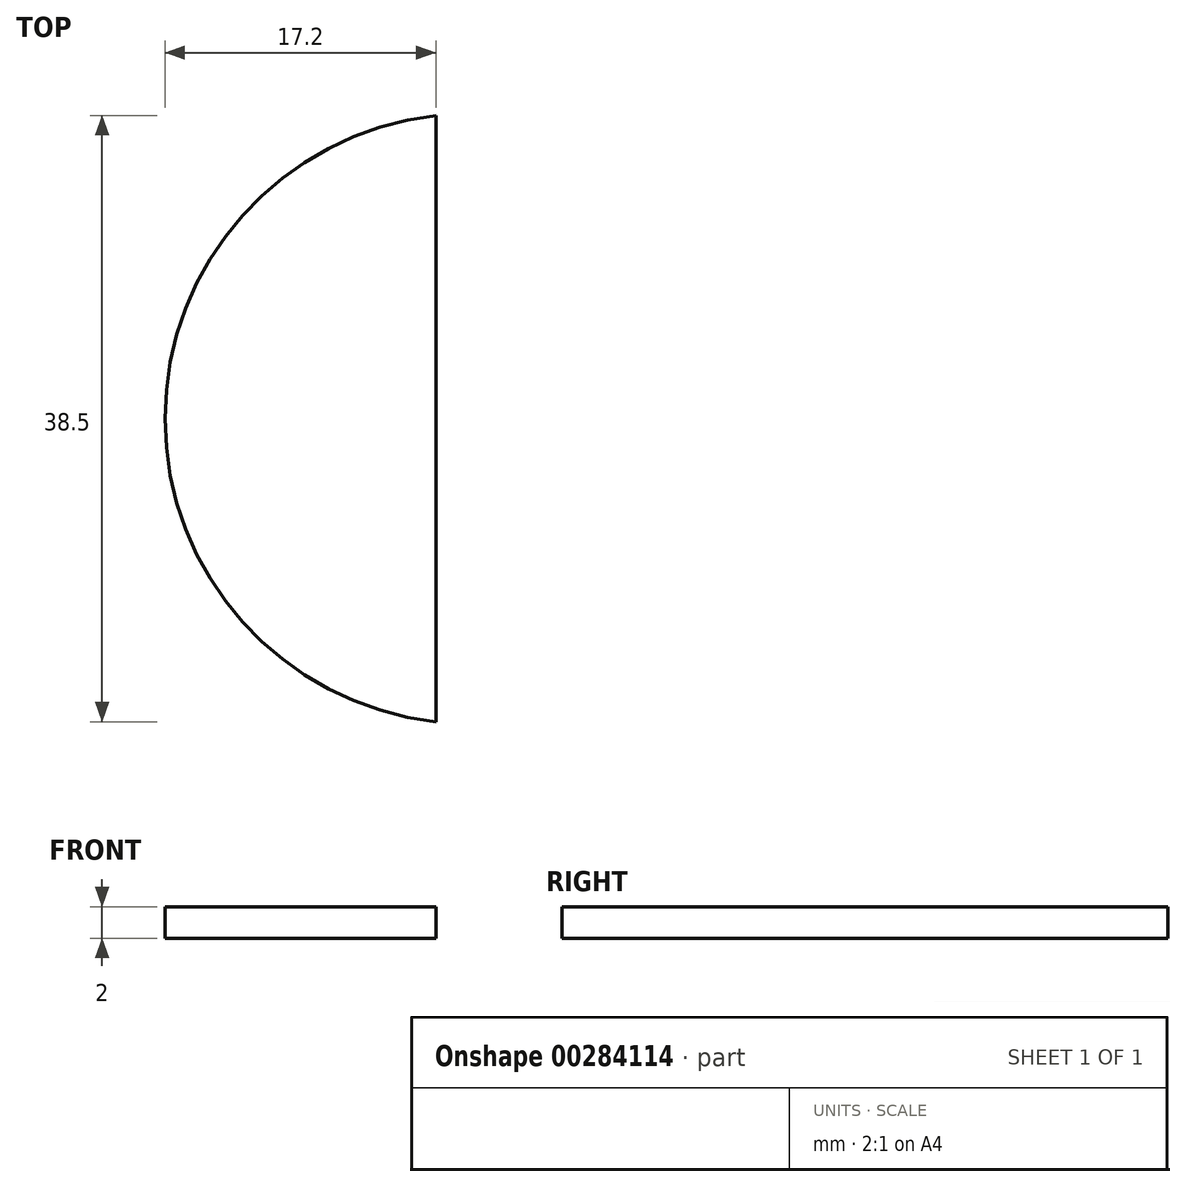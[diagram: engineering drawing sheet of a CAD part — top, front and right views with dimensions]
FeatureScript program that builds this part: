
annotation { "Feature Type Name" : "Feature", "Feature Type Description" : "" }
export const myFeature = defineFeature(function(context is Context, id is Id, definition is map)
    precondition{}
    {
        {
            var Q0;
            Q0=qCreatedBy(makeId("Top.planeOp"),FACE);
            var sketch = newSketch(context, id + "F0", { "sketchPlane" : qUnion([Q0])});
            skArc(sketch, "E0", {"start": v(0, 38.5) * mm, "mid": v(-17.2, 19.25) * mm, "end": v(0, 0) * mm});
            skLineSegment(sketch, "E1", {"start": v(0, 38.5) * mm, "end": v(0, 0) * mm});
            skSolve(sketch);
        }
        {
            var Q0;
            Q0=makeQuery(id+"F0.imprint","IMPRINT",FACE,{"disambiguationData":[TD([[makeQuery(id+"F0.imprint","IMPRINT",EDGE,{"derivedFrom":sQuery(id+"F0.wireOp",EDGE,"E0")}),1.0]])]});
            extrude(context, id + "F1", {"entities" : qUnion([Q0]), "depth" : 2 * mm});
        }
    });
